# Revit family: Bath-Freestanding-BubbleMassage-Heated_Surface-KOHLER-Sunstruck-K-24009_1
name_source: partatom
category: Plumbing Fixtures
units: mm (PartAtom-declared; Revit-internal decimal feet)

## family parameters
Cut with Voids When Loaded = No
Host = Face
OmniClass Number = 23.31.15.00
OmniClass Title = Bathtubs
Part Type = Normal
Room Calculation Point = No
Round Connector Dimension = Use Diameter
Shared = No

## types (2) — shared parameters
ADA Compliant = No
Amplifer Electrical Connector = Amplifer Electrical Connector
Apparent Load = 1800 VA
Assembly Code = D2010500
Blower Electrical Connector = Blower Electrical Connector
CW Connection = No
Cold Water Inlet = Cold Water Inlet
Date Modified = 03/24/2023
Default Elevation = 0"
Description = 60-1/2Inch x 34-1/2Inch Freestanding Heated BubbleMassage Air Bath With Bask Heated Surface And Fluted Shroud
Drain Included = No
Electrical Connector = Yes
Electrical Note = Two dedicated circuits required, protected with Class A GroundFault Circuit-Interrupter (GFCI). Outside North America, this
device may be known as a Residual Current Device (RCD).
HW Connection = No
Heater Electrical Connector = Heater Electrical Connector
Height = 25 15/16"
Hot Water Inlet = Hot Water Inlet
Length = 60 9/16"
Manufacturer = Kohler Co.
Master Format 2014 = 22 41 19
Master Format 2014 Name = Residential Bathtubs
Material = Acrylic
Product Documentation Link = https://www.us.kohler.com
Product Name = Sunstruck
Product Page URL = http://www.us.kohler.com
Pump Electrical Connector = Pump Electrical Connector
URL = https://www.us.kohler.com
Vent Connection = No
Voltage = 120 V
Waste Connection = Yes
Waste Water Outlet = Waste Water Outlet
WaterSense Certified = No
Width = 34 11/16"

## per-type parameters (varying)
| type | Finish | Model | Type |
| 0-White | KOHLER-Acrylic-0-White | K-24009-GHW-0 | 1 |
| 96-Biscuit | KOHLER-Acrylic-96-Biscuit | K-24009-GHW-96 | 2 |

## geometry (parser evidence)
native form markers: Sweep x5
no freeform markers — native parametric forms only
